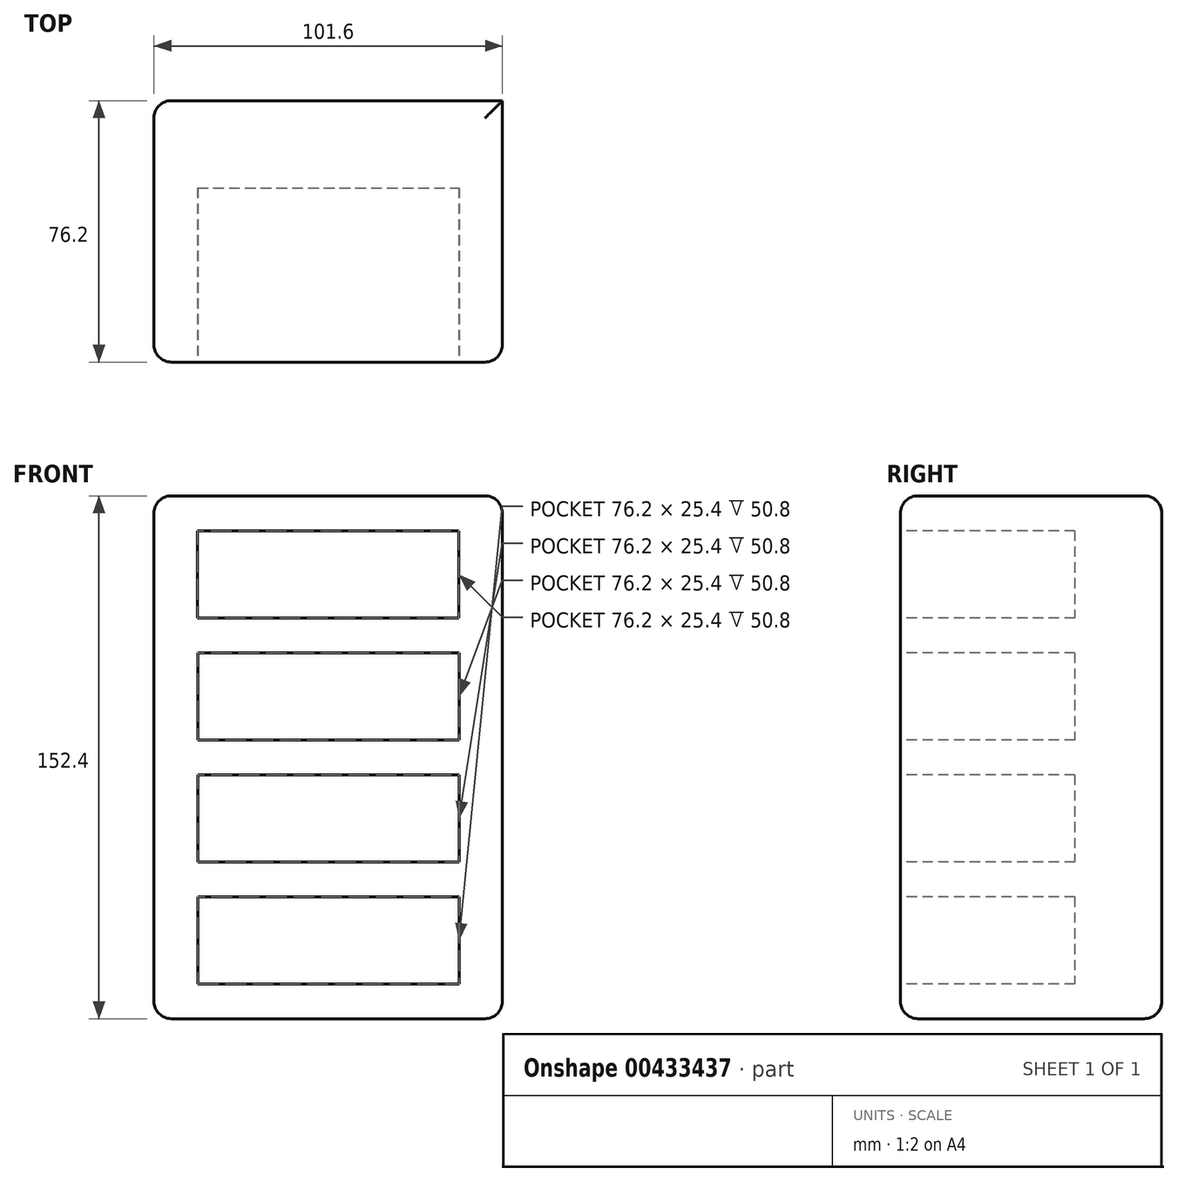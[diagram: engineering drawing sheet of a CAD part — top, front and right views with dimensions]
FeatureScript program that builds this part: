
annotation { "Feature Type Name" : "Feature", "Feature Type Description" : "" }
export const myFeature = defineFeature(function(context is Context, id is Id, definition is map)
    precondition{}
    {
        {
            var Q0;
            Q0=qCreatedBy(makeId("Top.planeOp"),FACE);
            var sketch = newSketch(context, id + "F0", { "sketchPlane" : qUnion([Q0])});
            skLineSegment(sketch, "E0.bottom", {"start": v(-50.09, 25.93) * mm, "end": v(51.51, 25.93) * mm});
            skLineSegment(sketch, "E0.top", {"start": v(-50.09, -50.27) * mm, "end": v(51.51, -50.27) * mm});
            skLineSegment(sketch, "E0.left", {"start": v(-50.09, 25.93) * mm, "end": v(-50.09, -50.27) * mm});
            skLineSegment(sketch, "E0.right", {"start": v(51.51, 25.93) * mm, "end": v(51.51, -50.27) * mm});
            skSolve(sketch);
        }
        {
            var Q0;
            Q0=makeQuery(id+"F0.imprint","IMPRINT",FACE,{"disambiguationData":[TD([[makeQuery(id+"F0.imprint","IMPRINT",EDGE,{"derivedFrom":sQuery(id+"F0.wireOp",EDGE,"E0.bottom")}),-1.0]])]});
            extrude(context, id + "F1", {"entities" : qUnion([Q0]), "depth" : 152.4 * mm});
        }
        {
            var Q0;
            Q0=makeQuery(id+"F1.opExtrude","SWEPT_FACE",FACE,{"disambiguationData":[OSD([sQuery(id+"F0.wireOp",EDGE,"E0.top")])]});
            var sketch = newSketch(context, id + "F2", { "sketchPlane" : qUnion([Q0])});
            skLineSegment(sketch, "E1.bottom", {"start": v(-37.39, 142.24) * mm, "end": v(38.81, 142.24) * mm});
            skLineSegment(sketch, "E1.top", {"start": v(-37.39, 116.84) * mm, "end": v(38.81, 116.84) * mm});
            skLineSegment(sketch, "E1.left", {"start": v(-37.39, 142.24) * mm, "end": v(-37.39, 116.84) * mm});
            skLineSegment(sketch, "E1.right", {"start": v(38.81, 142.24) * mm, "end": v(38.81, 116.84) * mm});
            skLineSegment(sketch, "E2.0.1.0", {"start": v(-37.34, 106.68) * mm, "end": v(38.86, 106.68) * mm});
            skLineSegment(sketch, "E2.0.1.1", {"start": v(-37.34, 106.68) * mm, "end": v(-37.34, 81.28) * mm});
            skLineSegment(sketch, "E2.0.1.2", {"start": v(-37.34, 81.28) * mm, "end": v(38.86, 81.28) * mm});
            skLineSegment(sketch, "E2.0.1.3", {"start": v(38.86, 106.68) * mm, "end": v(38.86, 81.28) * mm});
            skLineSegment(sketch, "E2.0.2.0", {"start": v(-37.29, 71.12) * mm, "end": v(38.91, 71.12) * mm});
            skLineSegment(sketch, "E2.0.2.1", {"start": v(-37.29, 71.12) * mm, "end": v(-37.29, 45.72) * mm});
            skLineSegment(sketch, "E2.0.2.2", {"start": v(-37.29, 45.72) * mm, "end": v(38.91, 45.72) * mm});
            skLineSegment(sketch, "E2.0.2.3", {"start": v(38.91, 71.12) * mm, "end": v(38.91, 45.72) * mm});
            skLineSegment(sketch, "E2.0.3.0", {"start": v(-37.24, 35.56) * mm, "end": v(38.96, 35.56) * mm});
            skLineSegment(sketch, "E2.0.3.1", {"start": v(-37.24, 35.56) * mm, "end": v(-37.24, 10.16) * mm});
            skLineSegment(sketch, "E2.0.3.2", {"start": v(-37.24, 10.16) * mm, "end": v(38.96, 10.16) * mm});
            skLineSegment(sketch, "E2.0.3.3", {"start": v(38.96, 35.56) * mm, "end": v(38.96, 10.16) * mm});
            skLineSegment(sketch, "E2.direction1", {"start": v(-37.39, 142.24) * mm, "end": v(-11.99, 142.24) * mm, "construction": true});
            skLineSegment(sketch, "E2.direction2", {"start": v(-37.39, 142.24) * mm, "end": v(-37.34, 106.68) * mm, "construction": true});
            skSolve(sketch);
        }
        {
            var Q0;
            Q0 = qSketchRegion(id + "F2", true);
            extrude(context, id + "F3", {"entities" : qUnion([Q0]), "operationType" : NewBodyOperationType.REMOVE, "oppositeDirection" : true, "depth" : 50.8 * mm});
        }
        {
            var Q0;
            Q0=makeQuery(id+"F1.opExtrude","CAP_EDGE",EDGE,{"disambiguationData":[OSD([sQuery(id+"F0.wireOp",EDGE,"E0.left")])],"isStart":false});
            var Q1;
            Q1=makeQuery(id+"F1.opExtrude","CAP_FACE",FACE,{"disambiguationData":[OSD([sQuery(id+"F0.wireOp",EDGE,"E0.bottom"),sQuery(id+"F0.wireOp",EDGE,"E0.top"),sQuery(id+"F0.wireOp",EDGE,"E0.left"),sQuery(id+"F0.wireOp",EDGE,"E0.right")])],"isStart":false});
            var Q2;
            Q2=makeQuery(id+"F1.opExtrude","CAP_EDGE",EDGE,{"disambiguationData":[OSD([sQuery(id+"F0.wireOp",EDGE,"E0.top")])],"isStart":false});
            var Q3;
            Q3=makeQuery(id+"F1.opExtrude","SWEPT_EDGE",EDGE,{"disambiguationData":[OSD([sQuery(id+"F0.wireOp",EDGE,"E0.top"),sQuery(id+"F0.wireOp",EDGE,"E0.right")])]});
            var Q4;
            Q4=makeQuery(id+"F1.opExtrude","SWEPT_EDGE",EDGE,{"disambiguationData":[OSD([sQuery(id+"F0.wireOp",EDGE,"E0.top"),sQuery(id+"F0.wireOp",EDGE,"E0.left")])]});
            var Q5;
            Q5=makeQuery(id+"F1.opExtrude","SWEPT_EDGE",EDGE,{"disambiguationData":[OSD([sQuery(id+"F0.wireOp",EDGE,"E0.bottom"),sQuery(id+"F0.wireOp",EDGE,"E0.left")])]});
            var Q6;
            Q6=makeQuery(id+"F1.opExtrude","CAP_EDGE",EDGE,{"disambiguationData":[OSD([sQuery(id+"F0.wireOp",EDGE,"E0.top")])],"isStart":true});
            var Q7;
            Q7=makeQuery(id+"F1.opExtrude","CAP_EDGE",EDGE,{"disambiguationData":[OSD([sQuery(id+"F0.wireOp",EDGE,"E0.right")])],"isStart":true});
            var Q8;
            Q8=makeQuery(id+"F1.opExtrude","CAP_EDGE",EDGE,{"disambiguationData":[OSD([sQuery(id+"F0.wireOp",EDGE,"E0.bottom")])],"isStart":true});
            var Q9;
            Q9=makeQuery(id+"F1.opExtrude","CAP_EDGE",EDGE,{"disambiguationData":[OSD([sQuery(id+"F0.wireOp",EDGE,"E0.left")])],"isStart":true});
            fillet(context, id + "F4", {"entities" : qUnion([Q0, Q1, Q2, Q3, Q4, Q5, Q6, Q7, Q8, Q9]), "radius" : 5.08 * mm, "tangentPropagation" : true, "allowEdgeOverflow" : false});
        }
    });
